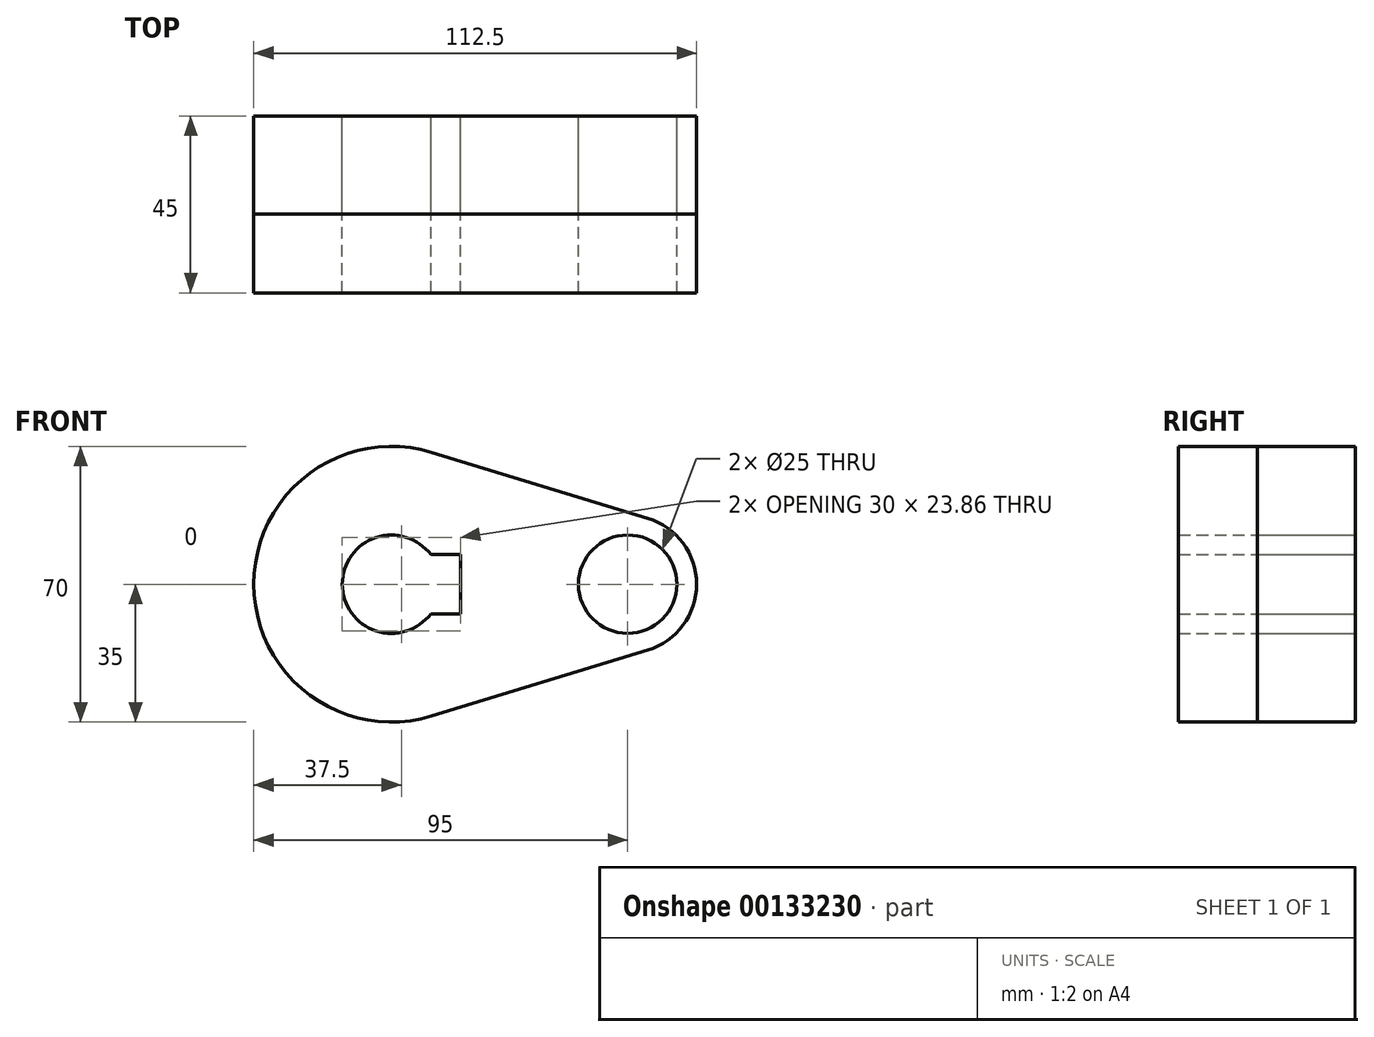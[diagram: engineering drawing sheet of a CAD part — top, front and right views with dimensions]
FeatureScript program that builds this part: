
annotation { "Feature Type Name" : "Feature", "Feature Type Description" : "" }
export const myFeature = defineFeature(function(context is Context, id is Id, definition is map)
    precondition{}
    {
        {
            var Q0;
            Q0=qCreatedBy(makeId("Front.planeOp"),FACE);
            var sketch = newSketch(context, id + "F0", { "sketchPlane" : qUnion([Q0])});
            skCircle(sketch, "E0", {"center": v(0, 0) * mm, "radius": 35 * mm});
            skCircle(sketch, "E1", {"center": v(60, 0) * mm, "radius": 17.5 * mm});
            skLineSegment(sketch, "E2", {"start": v(10.2, 33.48) * mm, "end": v(65.1, 16.74) * mm});
            skLineSegment(sketch, "E3", {"start": v(10.2, -33.48) * mm, "end": v(65.1, -16.74) * mm});
            skCircle(sketch, "E4", {"center": v(60, 0) * mm, "radius": 12.5 * mm});
            skCircle(sketch, "E5", {"center": v(0, 0) * mm, "radius": 12.5 * mm});
            skLineSegment(sketch, "E6.bottom", {"start": v(-17.5, -7.5) * mm, "end": v(17.5, -7.5) * mm});
            skLineSegment(sketch, "E6.top", {"start": v(-17.5, 7.5) * mm, "end": v(17.5, 7.5) * mm});
            skLineSegment(sketch, "E6.left", {"start": v(-17.5, -7.5) * mm, "end": v(-17.5, 7.5) * mm});
            skLineSegment(sketch, "E6.right", {"start": v(17.5, -7.5) * mm, "end": v(17.5, 7.5) * mm});
            skSolve(sketch);
        }
        {
            var Q0;
            {var subQ7=sQuery(id+"F0.wireOp",EDGE,"E6.left");Q0=makeQuery(id+"F0.imprint","IMPRINT",FACE,{"disambiguationData":[TD([[makeQuery(id+"F0.imprint","IMPRINT",EDGE,{"derivedFrom":subQ7}),1.0]])]});}
            var Q1;
            {var subQ5=sQuery(id+"F0.wireOp",EDGE,"E6.left");Q1=makeQuery(id+"F0.imprint","IMPRINT",FACE,{"disambiguationData":[TD([[makeQuery(id+"F0.imprint","IMPRINT",EDGE,{"derivedFrom":subQ5}),-1.0]])]});}
            var Q2;
            {var subQ0=sQuery(id+"F0.wireOp",EDGE,"E2");Q2=makeQuery(id+"F0.imprint","IMPRINT",FACE,{"disambiguationData":[TD([[makeQuery(id+"F0.imprint","IMPRINT",EDGE,{"derivedFrom":subQ0}),-1.0]])]});}
            var Q3;
            Q3=makeQuery(id+"F0.imprint","IMPRINT",FACE,{"disambiguationData":[TD([[makeQuery(id+"F0.imprint","IMPRINT",EDGE,{"derivedFrom":sQuery(id+"F0.wireOp",EDGE,"E4")}),-1.0]])]});
            extrude(context, id + "F1", {"entities" : qUnion([Q0, Q1, Q2, Q3]), "depth" : 25 * mm});
        }
        {
            var Q0;
            {var subQ7=sQuery(id+"F0.wireOp",EDGE,"E6.left");Q0=makeQuery(id+"F0.imprint","IMPRINT",FACE,{"disambiguationData":[TD([[makeQuery(id+"F0.imprint","IMPRINT",EDGE,{"derivedFrom":subQ7}),1.0]])]});}
            var Q1;
            {var subQ5=sQuery(id+"F0.wireOp",EDGE,"E6.left");Q1=makeQuery(id+"F0.imprint","IMPRINT",FACE,{"disambiguationData":[TD([[makeQuery(id+"F0.imprint","IMPRINT",EDGE,{"derivedFrom":subQ5}),-1.0]])]});}
            var Q2;
            {var subQ0=sQuery(id+"F0.wireOp",EDGE,"E2");Q2=makeQuery(id+"F0.imprint","IMPRINT",FACE,{"disambiguationData":[TD([[makeQuery(id+"F0.imprint","IMPRINT",EDGE,{"derivedFrom":subQ0}),-1.0]])]});}
            var Q3;
            Q3=makeQuery(id+"F0.imprint","IMPRINT",FACE,{"disambiguationData":[TD([[makeQuery(id+"F0.imprint","IMPRINT",EDGE,{"derivedFrom":sQuery(id+"F0.wireOp",EDGE,"E4")}),-1.0]])]});
            extrude(context, id + "F2", {"entities" : qUnion([Q0, Q1, Q2, Q3]), "depth" : 45 * mm});
        }
    });
